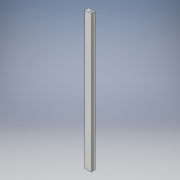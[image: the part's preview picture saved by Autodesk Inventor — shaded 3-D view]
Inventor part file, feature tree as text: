
AUTODESK INVENTOR PART (.ipt)
format: ipt  version: 2017 (Build 210142000, 142)  size: 102,912 bytes
history: native  units: in
note: dims shown in document units (in); Inventor stores cm internally (conversion verified against a paired STEP export)
features: extrude x1, sketch x1
ambient origin geometry x8: Origin, YZ Plane, XZ Plane, XY Plane, X Axis, Y Axis, Z Axis, Center Point
bodies: Solid1 (feature_tree)
feature tree (2):
  extrude  "Extrusion1"  Depth=0.25in
  sketch  "Sketch1"  dims[d0=1.0in d1=0.25in d2=0.5in d3=0.125in d4=1.0in d5=0.25in d6=22.0in d7=0.0in]
